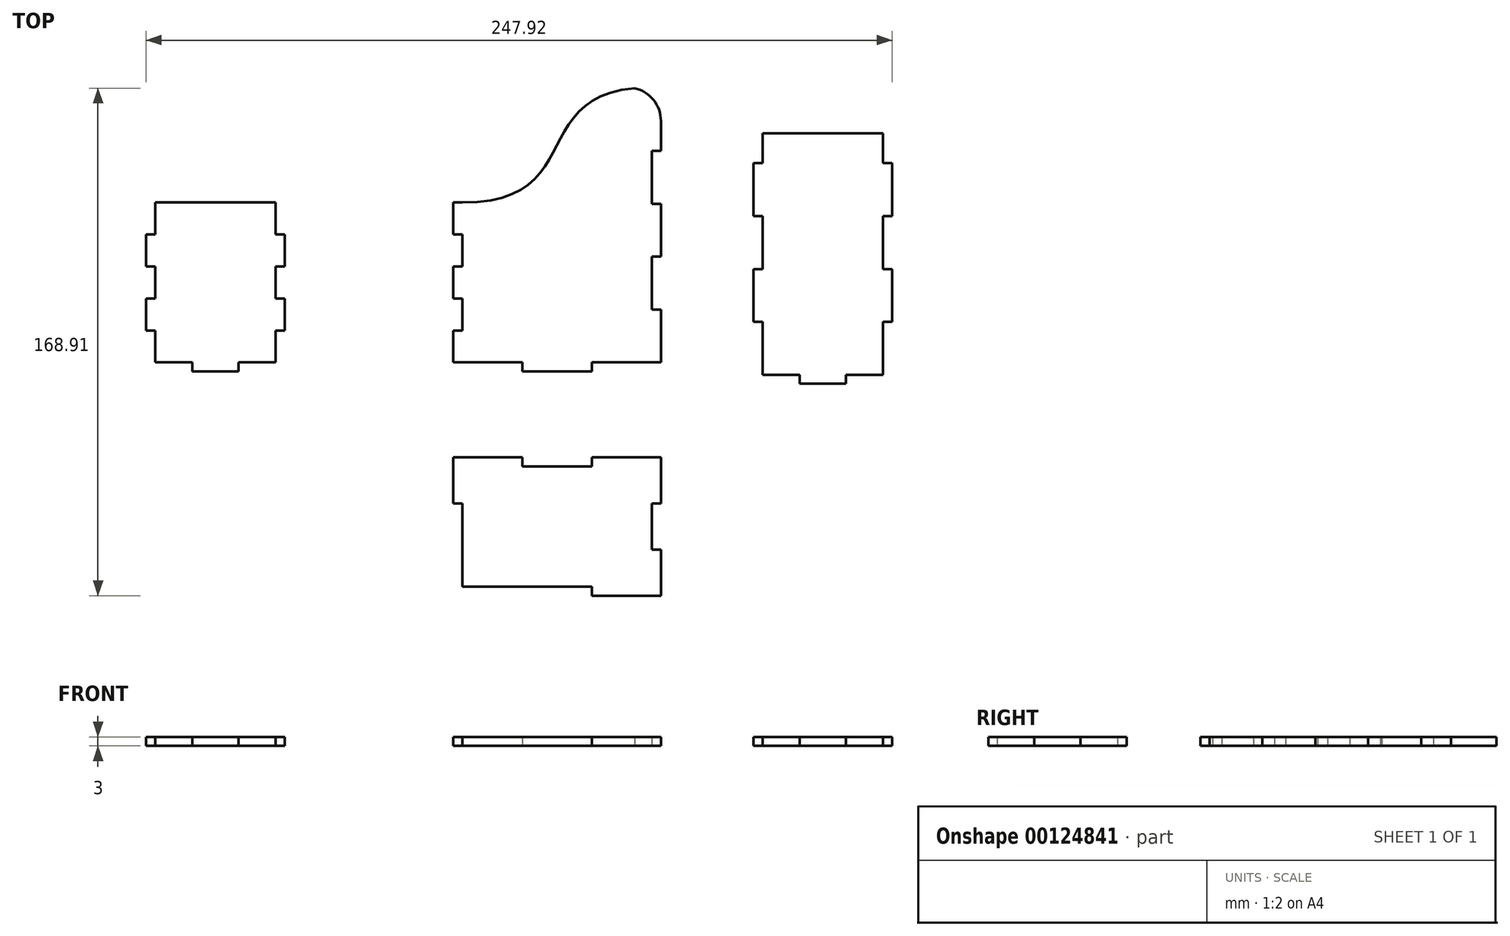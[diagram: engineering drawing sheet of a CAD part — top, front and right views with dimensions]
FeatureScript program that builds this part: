
annotation { "Feature Type Name" : "Feature", "Feature Type Description" : "" }
export const myFeature = defineFeature(function(context is Context, id is Id, definition is map)
    precondition{}
    {
        {
            var Q0;
            Q0=qCreatedBy(makeId("Top.planeOp"),FACE);
            var sketch = newSketch(context, id + "F0", { "sketchPlane" : qUnion([Q0])});
            skLineSegment(sketch, "E0", {"start": v(-70.06, 14.35) * mm, "end": v(-70.06, -38.88) * mm});
            skLineSegment(sketch, "E1", {"start": v(-70.06, -38.88) * mm, "end": v(-7.06, -38.88) * mm});
            skLineSegment(sketch, "E2", {"start": v(-7.06, -38.88) * mm, "end": v(-7.06, 49.12) * mm});
            skLineSegment(sketch, "E3", {"start": v(-172.16, 14.35) * mm, "end": v(-172.16, -38.88) * mm});
            skLineSegment(sketch, "E4", {"start": v(-172.16, -38.88) * mm, "end": v(-132.16, -38.88) * mm});
            skLineSegment(sketch, "E5", {"start": v(-132.16, 14.35) * mm, "end": v(-172.16, 14.35) * mm});
            skLineSegment(sketch, "E6", {"start": v(-70.06, -73.5) * mm, "end": v(-70.06, -113.5) * mm});
            skLineSegment(sketch, "E7", {"start": v(-70.06, -113.5) * mm, "end": v(-7.06, -113.5) * mm});
            skLineSegment(sketch, "E8", {"start": v(-7.06, -113.5) * mm, "end": v(-7.06, -73.5) * mm});
            skLineSegment(sketch, "E9", {"start": v(-7.06, -73.5) * mm, "end": v(-70.06, -73.5) * mm});
            skLineSegment(sketch, "E10", {"start": v(-132.16, 14.35) * mm, "end": v(-132.16, -38.88) * mm});
            skLineSegment(sketch, "E11", {"start": v(-70.06, 14.35) * mm, "end": v(-73.06, 14.35) * mm});
            skLineSegment(sketch, "E12", {"start": v(-73.06, 14.35) * mm, "end": v(-73.06, 3.7) * mm});
            skLineSegment(sketch, "E13", {"start": v(-73.06, 3.7) * mm, "end": v(-70.06, 3.7) * mm});
            skLineSegment(sketch, "E14", {"start": v(-70.06, -6.94) * mm, "end": v(-73.06, -6.94) * mm});
            skLineSegment(sketch, "E15", {"start": v(-73.06, -6.94) * mm, "end": v(-73.06, -17.59) * mm});
            skLineSegment(sketch, "E16", {"start": v(-73.06, -17.59) * mm, "end": v(-70.06, -17.59) * mm});
            skLineSegment(sketch, "E17", {"start": v(-70.06, -38.88) * mm, "end": v(-73.06, -38.88) * mm});
            skLineSegment(sketch, "E18", {"start": v(-73.06, -38.88) * mm, "end": v(-73.06, -28.23) * mm});
            skLineSegment(sketch, "E19", {"start": v(-73.06, -28.23) * mm, "end": v(-70.06, -28.23) * mm});
            skLineSegment(sketch, "E20", {"start": v(-73.06, 3.7) * mm, "end": v(-73.06, -6.94) * mm, "construction": true});
            skLineSegment(sketch, "E21", {"start": v(-73.06, -17.59) * mm, "end": v(-73.06, -28.23) * mm, "construction": true});
            skLineSegment(sketch, "E22", {"start": v(-132.16, 14.35) * mm, "end": v(-129.16, 14.35) * mm, "construction": true});
            skLineSegment(sketch, "E23", {"start": v(-129.16, 14.35) * mm, "end": v(-129.16, 3.7) * mm, "construction": true});
            skLineSegment(sketch, "E24", {"start": v(-129.16, -38.88) * mm, "end": v(-132.16, -38.88) * mm, "construction": true});
            skLineSegment(sketch, "E25", {"start": v(-132.16, 3.7) * mm, "end": v(-129.16, 3.7) * mm});
            skLineSegment(sketch, "E26", {"start": v(-132.16, -6.94) * mm, "end": v(-129.16, -6.94) * mm});
            skLineSegment(sketch, "E27", {"start": v(-132.16, -17.59) * mm, "end": v(-129.16, -17.59) * mm});
            skLineSegment(sketch, "E28", {"start": v(-132.16, -28.23) * mm, "end": v(-129.16, -28.23) * mm});
            skLineSegment(sketch, "E29", {"start": v(-129.16, 3.7) * mm, "end": v(-129.16, -6.94) * mm});
            skLineSegment(sketch, "E30", {"start": v(-129.16, -6.94) * mm, "end": v(-129.16, -17.59) * mm, "construction": true});
            skLineSegment(sketch, "E31", {"start": v(-129.16, -17.59) * mm, "end": v(-129.16, -28.23) * mm});
            skLineSegment(sketch, "E32", {"start": v(-129.16, -28.23) * mm, "end": v(-129.16, -38.88) * mm, "construction": true});
            skLineSegment(sketch, "E33", {"start": v(-7.06, 52.67) * mm, "end": v(-4.06, 52.67) * mm, "construction": true});
            skLineSegment(sketch, "E34", {"start": v(-4.06, 52.67) * mm, "end": v(-4.06, 41.5) * mm, "construction": true});
            skLineSegment(sketch, "E35", {"start": v(-4.06, -38.88) * mm, "end": v(-7.06, -38.88) * mm});
            skLineSegment(sketch, "E36", {"start": v(-7.06, 31.52) * mm, "end": v(-4.06, 31.52) * mm});
            skLineSegment(sketch, "E37", {"start": v(-7.06, 13.92) * mm, "end": v(-4.06, 13.92) * mm});
            skLineSegment(sketch, "E38", {"start": v(-7.06, -3.68) * mm, "end": v(-4.06, -3.68) * mm});
            skLineSegment(sketch, "E39", {"start": v(-7.06, -21.28) * mm, "end": v(-4.06, -21.28) * mm});
            skLineSegment(sketch, "E40", {"start": v(-4.06, 31.52) * mm, "end": v(-4.06, 13.92) * mm, "construction": true});
            skLineSegment(sketch, "E41", {"start": v(-4.06, 13.92) * mm, "end": v(-4.06, -3.68) * mm});
            skLineSegment(sketch, "E42", {"start": v(-4.06, -3.68) * mm, "end": v(-4.06, -21.28) * mm, "construction": true});
            skLineSegment(sketch, "E43", {"start": v(-4.06, -21.28) * mm, "end": v(-4.06, -38.88) * mm});
            skLineSegment(sketch, "E44", {"start": v(-73.06, -38.88) * mm, "end": v(-73.06, -41.88) * mm, "construction": true});
            skLineSegment(sketch, "E45", {"start": v(-73.06, -41.88) * mm, "end": v(-50.06, -41.88) * mm, "construction": true});
            skLineSegment(sketch, "E46", {"start": v(-4.06, -41.88) * mm, "end": v(-4.06, -38.88) * mm, "construction": true});
            skLineSegment(sketch, "E47", {"start": v(-50.06, -38.88) * mm, "end": v(-50.06, -41.88) * mm});
            skLineSegment(sketch, "E48", {"start": v(-27.06, -38.88) * mm, "end": v(-27.06, -41.88) * mm});
            skLineSegment(sketch, "E49", {"start": v(-50.06, -41.88) * mm, "end": v(-27.06, -41.88) * mm});
            skLineSegment(sketch, "E50", {"start": v(-27.06, -41.88) * mm, "end": v(-4.06, -41.88) * mm, "construction": true});
            skLineSegment(sketch, "E51.bottom", {"start": v(-73.06, -70.5) * mm, "end": v(-50.06, -70.5) * mm});
            skLineSegment(sketch, "E51.left", {"start": v(-73.06, -70.5) * mm, "end": v(-73.06, -85.83) * mm});
            skLineSegment(sketch, "E52", {"start": v(-70.06, -73.5) * mm, "end": v(-73.06, -73.5) * mm, "construction": true});
            skLineSegment(sketch, "E53", {"start": v(-70.06, -73.5) * mm, "end": v(-70.06, -70.5) * mm, "construction": true});
            skLineSegment(sketch, "E54", {"start": v(-70.06, -113.5) * mm, "end": v(-73.06, -113.5) * mm, "construction": true});
            skLineSegment(sketch, "E55", {"start": v(-73.06, -113.5) * mm, "end": v(-70.06, -113.5) * mm, "construction": true});
            skLineSegment(sketch, "E56", {"start": v(-70.06, -113.5) * mm, "end": v(-70.06, -116.5) * mm, "construction": true});
            skLineSegment(sketch, "E57", {"start": v(-7.06, -113.5) * mm, "end": v(-7.06, -116.5) * mm, "construction": true});
            skLineSegment(sketch, "E58", {"start": v(-7.06, -113.5) * mm, "end": v(-4.06, -113.5) * mm, "construction": true});
            skLineSegment(sketch, "E59", {"start": v(-7.06, -73.5) * mm, "end": v(-4.06, -73.5) * mm, "construction": true});
            skLineSegment(sketch, "E60", {"start": v(-7.06, -73.5) * mm, "end": v(-7.06, -70.5) * mm, "construction": true});
            skLineSegment(sketch, "E61", {"start": v(-50.06, -70.5) * mm, "end": v(-50.06, -73.5) * mm});
            skLineSegment(sketch, "E62", {"start": v(-27.06, -70.5) * mm, "end": v(-27.06, -73.5) * mm});
            skPoint(sketch, "E62.endSnap0", {"position": v(-38.56, -73.5) * mm});
            skLineSegment(sketch, "E63", {"start": v(-50.06, -70.5) * mm, "end": v(-27.06, -70.5) * mm, "construction": true});
            skLineSegment(sketch, "E64", {"start": v(-27.06, -70.5) * mm, "end": v(-4.06, -70.5) * mm});
            skLineSegment(sketch, "E65", {"start": v(-73.06, -85.83) * mm, "end": v(-70.06, -85.83) * mm});
            skLineSegment(sketch, "E66", {"start": v(-73.06, -101.16) * mm, "end": v(-70.06, -101.16) * mm});
            skLineSegment(sketch, "E67", {"start": v(-73.06, -85.83) * mm, "end": v(-73.06, -101.16) * mm, "construction": true});
            skLineSegment(sketch, "E68", {"start": v(-73.06, -101.16) * mm, "end": v(-73.06, -116.5) * mm});
            skLineSegment(sketch, "E69", {"start": v(-70.06, -93.5) * mm, "end": v(-7.06, -93.5) * mm, "construction": true});
            skLineSegment(sketch, "E70", {"start": v(-38.56, -113.5) * mm, "end": v(-38.56, -73.5) * mm, "construction": true});
            skLineSegment(sketch, "E71.MirrorCS", {"start": v(-4.06, -113.5) * mm, "end": v(-7.06, -113.5) * mm, "construction": true});
            skLineSegment(sketch, "E72.MirrorCS", {"start": v(-4.06, -85.83) * mm, "end": v(-7.06, -85.83) * mm});
            skLineSegment(sketch, "E73.MirrorCS", {"start": v(-4.06, -101.16) * mm, "end": v(-7.06, -101.16) * mm});
            skLineSegment(sketch, "E74.MirrorCS", {"start": v(-4.06, -70.5) * mm, "end": v(-4.06, -85.83) * mm});
            skLineSegment(sketch, "E75.MirrorCS", {"start": v(-7.06, -73.5) * mm, "end": v(-7.06, -113.5) * mm});
            skLineSegment(sketch, "E76.MirrorCS", {"start": v(-4.06, -101.16) * mm, "end": v(-4.06, -116.5) * mm});
            skLineSegment(sketch, "E77", {"start": v(-4.06, -85.83) * mm, "end": v(-4.06, -101.16) * mm, "construction": true});
            skLineSegment(sketch, "E78.MirrorCS", {"start": v(-50.06, -116.5) * mm, "end": v(-50.06, -113.5) * mm});
            skLineSegment(sketch, "E79.MirrorCS", {"start": v(-27.06, -116.5) * mm, "end": v(-27.06, -113.5) * mm});
            skLineSegment(sketch, "E80.MirrorCS", {"start": v(-73.06, -116.5) * mm, "end": v(-73.06, -101.16) * mm});
            skLineSegment(sketch, "E81.MirrorCS", {"start": v(-73.06, -116.5) * mm, "end": v(-50.06, -116.5) * mm});
            skPoint(sketch, "E82.MirrorP", {"position": v(-38.56, -113.5) * mm});
            skLineSegment(sketch, "E83.MirrorCS", {"start": v(-7.06, -113.5) * mm, "end": v(-70.06, -113.5) * mm});
            skLineSegment(sketch, "E84.MirrorCS", {"start": v(-27.06, -116.5) * mm, "end": v(-4.06, -116.5) * mm});
            skLineSegment(sketch, "E85.MirrorCS", {"start": v(-4.06, -116.5) * mm, "end": v(-4.06, -101.16) * mm});
            skLineSegment(sketch, "E86.MirrorCS", {"start": v(-50.06, -116.5) * mm, "end": v(-27.06, -116.5) * mm, "construction": true});
            skLineSegment(sketch, "E87", {"start": v(-172.16, 14.35) * mm, "end": v(-175.16, 14.35) * mm, "construction": true});
            skLineSegment(sketch, "E88", {"start": v(-175.16, 14.35) * mm, "end": v(-175.16, 3.7) * mm, "construction": true});
            skLineSegment(sketch, "E89", {"start": v(-175.16, -38.88) * mm, "end": v(-172.16, -38.88) * mm, "construction": true});
            skLineSegment(sketch, "E90", {"start": v(-175.16, 3.7) * mm, "end": v(-172.16, 3.7) * mm});
            skLineSegment(sketch, "E91", {"start": v(-172.16, -6.94) * mm, "end": v(-175.16, -6.94) * mm});
            skLineSegment(sketch, "E92", {"start": v(-175.16, -17.59) * mm, "end": v(-172.16, -17.59) * mm});
            skLineSegment(sketch, "E93", {"start": v(-172.16, -28.23) * mm, "end": v(-175.16, -28.23) * mm});
            skLineSegment(sketch, "E94", {"start": v(-175.16, 3.7) * mm, "end": v(-175.16, -6.94) * mm});
            skLineSegment(sketch, "E95", {"start": v(-175.16, -6.94) * mm, "end": v(-175.16, -17.59) * mm, "construction": true});
            skLineSegment(sketch, "E96", {"start": v(-175.16, -17.59) * mm, "end": v(-175.16, -28.23) * mm});
            skLineSegment(sketch, "E97", {"start": v(-175.16, -28.23) * mm, "end": v(-175.16, -38.88) * mm, "construction": true});
            skLineSegment(sketch, "E98", {"start": v(-175.16, -38.88) * mm, "end": v(-175.16, -41.88) * mm, "construction": true});
            skLineSegment(sketch, "E99", {"start": v(-175.16, -41.88) * mm, "end": v(-159.83, -41.88) * mm, "construction": true});
            skLineSegment(sketch, "E100", {"start": v(-129.16, -41.88) * mm, "end": v(-129.16, -38.88) * mm, "construction": true});
            skLineSegment(sketch, "E101", {"start": v(-159.83, -38.88) * mm, "end": v(-159.83, -41.88) * mm});
            skLineSegment(sketch, "E102", {"start": v(-144.5, -38.88) * mm, "end": v(-144.5, -41.88) * mm});
            skLineSegment(sketch, "E103", {"start": v(-159.83, -41.88) * mm, "end": v(-144.5, -41.88) * mm});
            skLineSegment(sketch, "E104", {"start": v(-144.5, -41.88) * mm, "end": v(-129.16, -41.88) * mm, "construction": true});
            skLineSegment(sketch, "E105.bottom", {"start": v(29.76, 37.42) * mm, "end": v(69.76, 37.42) * mm});
            skLineSegment(sketch, "E105.top", {"start": v(29.76, -42.97) * mm, "end": v(69.76, -42.97) * mm});
            skLineSegment(sketch, "E105.left", {"start": v(29.76, 37.42) * mm, "end": v(29.76, -42.97) * mm});
            skLineSegment(sketch, "E106", {"start": v(29.76, 37.42) * mm, "end": v(26.76, 37.42) * mm, "construction": true});
            skLineSegment(sketch, "E107", {"start": v(26.76, 37.42) * mm, "end": v(26.76, 27.43) * mm, "construction": true});
            skLineSegment(sketch, "E108", {"start": v(26.76, -42.97) * mm, "end": v(29.76, -42.97) * mm, "construction": true});
            skLineSegment(sketch, "E109", {"start": v(26.76, 27.43) * mm, "end": v(29.76, 27.43) * mm});
            skLineSegment(sketch, "E110", {"start": v(26.76, 9.83) * mm, "end": v(29.76, 9.83) * mm});
            skLineSegment(sketch, "E111", {"start": v(26.76, -7.77) * mm, "end": v(29.76, -7.77) * mm});
            skLineSegment(sketch, "E112", {"start": v(26.76, -25.37) * mm, "end": v(29.76, -25.37) * mm});
            skLineSegment(sketch, "E113", {"start": v(26.76, 27.43) * mm, "end": v(26.76, 9.83) * mm});
            skLineSegment(sketch, "E114", {"start": v(26.76, 9.83) * mm, "end": v(26.76, -7.77) * mm, "construction": true});
            skLineSegment(sketch, "E115", {"start": v(26.76, -7.77) * mm, "end": v(26.76, -25.37) * mm});
            skLineSegment(sketch, "E116", {"start": v(26.76, -25.37) * mm, "end": v(26.76, -42.97) * mm, "construction": true});
            skLineSegment(sketch, "E117.MirrorCS", {"start": v(69.76, 37.42) * mm, "end": v(69.76, -42.97) * mm});
            skLineSegment(sketch, "E118.MirrorCS", {"start": v(72.76, -7.77) * mm, "end": v(69.76, -7.77) * mm});
            skLineSegment(sketch, "E119.MirrorCS", {"start": v(72.76, 27.43) * mm, "end": v(69.76, 27.43) * mm});
            skLineSegment(sketch, "E120.MirrorCS", {"start": v(72.76, -25.37) * mm, "end": v(69.76, -25.37) * mm});
            skLineSegment(sketch, "E121.MirrorCS", {"start": v(72.76, 37.42) * mm, "end": v(72.76, 27.43) * mm, "construction": true});
            skLineSegment(sketch, "E122.MirrorCS", {"start": v(72.76, 9.83) * mm, "end": v(72.76, -7.77) * mm, "construction": true});
            skLineSegment(sketch, "E123.MirrorCS", {"start": v(72.76, 9.83) * mm, "end": v(69.76, 9.83) * mm});
            skLineSegment(sketch, "E124.MirrorCS", {"start": v(69.76, 37.42) * mm, "end": v(72.76, 37.42) * mm, "construction": true});
            skLineSegment(sketch, "E125.MirrorCS", {"start": v(72.76, 27.43) * mm, "end": v(72.76, 9.83) * mm});
            skLineSegment(sketch, "E126.MirrorCS", {"start": v(72.76, -25.37) * mm, "end": v(72.76, -42.97) * mm, "construction": true});
            skLineSegment(sketch, "E127.MirrorCS", {"start": v(72.76, -7.77) * mm, "end": v(72.76, -25.37) * mm});
            skLineSegment(sketch, "E128", {"start": v(26.76, -42.97) * mm, "end": v(26.76, -45.97) * mm, "construction": true});
            skLineSegment(sketch, "E129", {"start": v(26.76, -45.97) * mm, "end": v(42.09, -45.97) * mm, "construction": true});
            skLineSegment(sketch, "E130", {"start": v(72.76, -45.97) * mm, "end": v(72.76, -42.97) * mm, "construction": true});
            skLineSegment(sketch, "E131", {"start": v(42.09, -42.97) * mm, "end": v(42.09, -45.97) * mm});
            skLineSegment(sketch, "E132", {"start": v(57.42, -42.97) * mm, "end": v(57.42, -45.97) * mm});
            skLineSegment(sketch, "E133", {"start": v(42.09, -45.97) * mm, "end": v(57.42, -45.97) * mm});
            skLineSegment(sketch, "E134", {"start": v(57.42, -45.97) * mm, "end": v(72.76, -45.97) * mm, "construction": true});
            skLineSegment(sketch, "E135", {"start": v(72.76, -42.97) * mm, "end": v(69.76, -42.97) * mm, "construction": true});
            skFitSpline(sketch, "E136", {"points": [v(-70.06, 14.35) * mm, v(-7.06, 52.67) * mm], "startDerivative": vector(129, 0) * mm, "endDerivative": vector(129, 0) * mm});
            skPoint(sketch, "E137", {"position": v(-15.22, 41.5) * mm});
            skLineSegment(sketch, "E138", {"start": v(-73.06, 14.35) * mm, "end": v(-73.06, 99.35) * mm, "construction": true});
            skLineSegment(sketch, "E139", {"start": v(-73.06, 99.35) * mm, "end": v(84.8, 99.35) * mm, "construction": true});
            skCircle(sketch, "E140", {"center": v(-15.22, 41.5) * mm, "radius": 57.84 * mm, "construction": true});
            skLineSegment(sketch, "E141", {"start": v(-7.06, 52.67) * mm, "end": v(-73.06, 52.67) * mm, "construction": true});
            skLineSegment(sketch, "E142", {"start": v(-15.22, 41.5) * mm, "end": v(-15.22, 52.67) * mm, "construction": true});
            skLineSegment(sketch, "E143", {"start": v(-15.22, 41.5) * mm, "end": v(-4.06, 41.5) * mm, "construction": true});
            skCircle(sketch, "E144", {"center": v(-15.22, 41.5) * mm, "radius": 5.16 * mm, "construction": true});
            skArc(sketch, "E145", {"start": v(-12.83, 52.4) * mm, "mid": v(-23.91, 34.51) * mm, "end": v(-4.06, 41.5) * mm, "construction": true});
            skArc(sketch, "E146", {"start": v(-7.06, 49.12) * mm, "mid": v(-9.7, 51.2) * mm, "end": v(-12.83, 52.4) * mm});
            skFitSpline(sketch, "E147", {"points": [v(-70.06, 14.35) * mm, v(-7.06, 52.67) * mm], "startDerivative": vector(129, 0) * mm, "endDerivative": vector(129, 0) * mm, "construction": true});
            skLineSegment(sketch, "E148", {"start": v(-7.06, 49.12) * mm, "end": v(-7.06, 52.67) * mm, "construction": true});
            skArc(sketch, "E149", {"start": v(-4.06, 41.5) * mm, "mid": v(-4.83, 45.6) * mm, "end": v(-7.06, 49.12) * mm});
            skLineSegment(sketch, "E150", {"start": v(-4.06, 41.5) * mm, "end": v(-4.06, 31.52) * mm});
            skLineSegment(sketch, "E151", {"start": v(-70.06, 14.35) * mm, "end": v(-70.06, 52.67) * mm, "construction": true});
            skSolve(sketch);
        }
        {
            var Q0;
            {var subQ0=sQuery(id+"F0.wireOp",EDGE,"E119.MirrorCS");Q0=makeQuery(id+"F0.imprint","IMPRINT",FACE,{"disambiguationData":[TD([[makeQuery(id+"F0.imprint","IMPRINT",EDGE,{"derivedFrom":subQ0}),1.0]])]});}
            var Q1;
            {var subQ0=sQuery(id+"F0.wireOp",EDGE,"E118.MirrorCS");Q1=makeQuery(id+"F0.imprint","IMPRINT",FACE,{"disambiguationData":[TD([[makeQuery(id+"F0.imprint","IMPRINT",EDGE,{"derivedFrom":subQ0}),1.0]])]});}
            var Q2;
            {var subQ4=sQuery(id+"F0.wireOp",EDGE,"E9");var subQ5=sQuery(id+"F0.wireOp",EDGE,"E6");var subQ6=makeQuery(id+"F0.imprint","INTERSECT",VERTEX,{"derivedFrom":[subQ5,subQ4]});Q2=makeQuery(id+"F0.imprint","IMPRINT",FACE,{"disambiguationData":[TD([[makeQuery(id+"F0.imprint","IMPRINT",EDGE,{"disambiguationData":[TD([[subQ6,-1.0]])],"derivedFrom":subQ5}),1.0]])]});}
            var Q3;
            {var subQ1=sQuery(id+"F0.wireOp",EDGE,"E5");Q3=makeQuery(id+"F0.imprint","IMPRINT",FACE,{"disambiguationData":[TD([[makeQuery(id+"F0.imprint","IMPRINT",EDGE,{"derivedFrom":subQ1}),1.0]])]});}
            var Q4;
            {var subQ3=sQuery(id+"F0.wireOp",EDGE,"E79.MirrorCS");Q4=makeQuery(id+"F0.imprint","IMPRINT",FACE,{"disambiguationData":[TD([[makeQuery(id+"F0.imprint","IMPRINT",EDGE,{"derivedFrom":subQ3}),-1.0]])]});}
            var Q5;
            {var subQ0=sQuery(id+"F0.wireOp",EDGE,"E25");Q5=makeQuery(id+"F0.imprint","IMPRINT",FACE,{"disambiguationData":[TD([[makeQuery(id+"F0.imprint","IMPRINT",EDGE,{"derivedFrom":subQ0}),-1.0]])]});}
            var Q6;
            {var subQ0=sQuery(id+"F0.wireOp",EDGE,"E27");Q6=makeQuery(id+"F0.imprint","IMPRINT",FACE,{"disambiguationData":[TD([[makeQuery(id+"F0.imprint","IMPRINT",EDGE,{"derivedFrom":subQ0}),-1.0]])]});}
            var Q7;
            {var subQ0=sQuery(id+"F0.wireOp",EDGE,"E131");Q7=makeQuery(id+"F0.imprint","IMPRINT",FACE,{"disambiguationData":[TD([[makeQuery(id+"F0.imprint","IMPRINT",EDGE,{"derivedFrom":subQ0}),1.0]])]});}
            var Q8;
            {var subQ0=sQuery(id+"F0.wireOp",EDGE,"E11");Q8=makeQuery(id+"F0.imprint","IMPRINT",FACE,{"disambiguationData":[TD([[makeQuery(id+"F0.imprint","IMPRINT",EDGE,{"derivedFrom":subQ0}),1.0]])]});}
            var Q9;
            {var subQ0=sQuery(id+"F0.wireOp",EDGE,"E14");Q9=makeQuery(id+"F0.imprint","IMPRINT",FACE,{"disambiguationData":[TD([[makeQuery(id+"F0.imprint","IMPRINT",EDGE,{"derivedFrom":subQ0}),1.0]])]});}
            var Q10;
            {var subQ0=sQuery(id+"F0.wireOp",EDGE,"E17");Q10=makeQuery(id+"F0.imprint","IMPRINT",FACE,{"disambiguationData":[TD([[makeQuery(id+"F0.imprint","IMPRINT",EDGE,{"derivedFrom":subQ0}),-1.0]])]});}
            var Q11;
            {var subQ0=sQuery(id+"F0.wireOp",EDGE,"E47");Q11=makeQuery(id+"F0.imprint","IMPRINT",FACE,{"disambiguationData":[TD([[makeQuery(id+"F0.imprint","IMPRINT",EDGE,{"derivedFrom":subQ0}),1.0]])]});}
            var Q12;
            {var subQ0=sQuery(id+"F0.wireOp",EDGE,"E35");Q12=makeQuery(id+"F0.imprint","IMPRINT",FACE,{"disambiguationData":[TD([[makeQuery(id+"F0.imprint","IMPRINT",EDGE,{"derivedFrom":subQ0}),-1.0]])]});}
            var Q13;
            {var subQ0=sQuery(id+"F0.wireOp",EDGE,"E37");Q13=makeQuery(id+"F0.imprint","IMPRINT",FACE,{"disambiguationData":[TD([[makeQuery(id+"F0.imprint","IMPRINT",EDGE,{"derivedFrom":subQ0}),-1.0]])]});}
            var Q14;
            {var subQ2=sQuery(id+"F0.wireOp",EDGE,"E36");Q14=makeQuery(id+"F0.imprint","IMPRINT",FACE,{"disambiguationData":[TD([[makeQuery(id+"F0.imprint","IMPRINT",EDGE,{"derivedFrom":subQ2}),1.0]])]});}
            var Q15;
            {var subQ0=sQuery(id+"F0.wireOp",EDGE,"E90");Q15=makeQuery(id+"F0.imprint","IMPRINT",FACE,{"disambiguationData":[TD([[makeQuery(id+"F0.imprint","IMPRINT",EDGE,{"derivedFrom":subQ0}),-1.0]])]});}
            var Q16;
            {var subQ0=sQuery(id+"F0.wireOp",EDGE,"E92");Q16=makeQuery(id+"F0.imprint","IMPRINT",FACE,{"disambiguationData":[TD([[makeQuery(id+"F0.imprint","IMPRINT",EDGE,{"derivedFrom":subQ0}),-1.0]])]});}
            var Q17;
            {var subQ0=sQuery(id+"F0.wireOp",EDGE,"E101");Q17=makeQuery(id+"F0.imprint","IMPRINT",FACE,{"disambiguationData":[TD([[makeQuery(id+"F0.imprint","IMPRINT",EDGE,{"derivedFrom":subQ0}),1.0]])]});}
            var Q18;
            Q18=makeQuery(id+"F0.imprint","IMPRINT",FACE,{"disambiguationData":[TD([[makeQuery(id+"F0.imprint","IMPRINT",EDGE,{"derivedFrom":sQuery(id+"F0.wireOp",EDGE,"E51.bottom")}),-1.0]])]});
            var Q19;
            {var subQ1=sQuery(id+"F0.wireOp",EDGE,"E66");Q19=makeQuery(id+"F0.imprint","IMPRINT",FACE,{"disambiguationData":[TD([[makeQuery(id+"F0.imprint","IMPRINT",EDGE,{"derivedFrom":subQ1}),-1.0]])]});}
            var Q20;
            {var subQ1=sQuery(id+"F0.wireOp",EDGE,"E62");Q20=makeQuery(id+"F0.imprint","IMPRINT",FACE,{"disambiguationData":[TD([[makeQuery(id+"F0.imprint","IMPRINT",EDGE,{"derivedFrom":subQ1}),1.0]])]});}
            var Q21;
            {var subQ3=sQuery(id+"F0.wireOp",EDGE,"E105.bottom");Q21=makeQuery(id+"F0.imprint","IMPRINT",FACE,{"disambiguationData":[TD([[makeQuery(id+"F0.imprint","IMPRINT",EDGE,{"derivedFrom":subQ3}),-1.0]])]});}
            var Q22;
            {var subQ0=sQuery(id+"F0.wireOp",EDGE,"E109");Q22=makeQuery(id+"F0.imprint","IMPRINT",FACE,{"disambiguationData":[TD([[makeQuery(id+"F0.imprint","IMPRINT",EDGE,{"derivedFrom":subQ0}),-1.0]])]});}
            var Q23;
            {var subQ4=sQuery(id+"F0.wireOp",EDGE,"E136");Q23=makeQuery(id+"F0.imprint","IMPRINT",FACE,{"disambiguationData":[TD([[makeQuery(id+"F0.imprint","IMPRINT",EDGE,{"derivedFrom":subQ4}),-1.0]])]});}
            var Q24;
            {var subQ0=sQuery(id+"F0.wireOp",EDGE,"E111");Q24=makeQuery(id+"F0.imprint","IMPRINT",FACE,{"disambiguationData":[TD([[makeQuery(id+"F0.imprint","IMPRINT",EDGE,{"derivedFrom":subQ0}),-1.0]])]});}
            extrude(context, id + "F1", {"entities" : qUnion([Q0, Q1, Q2, Q3, Q4, Q5, Q6, Q7, Q8, Q9, Q10, Q11, Q12, Q13, Q14, Q15, Q16, Q17, Q18, Q19, Q20, Q21, Q22, Q23, Q24]), "depth" : 3 * mm});
        }
    });
